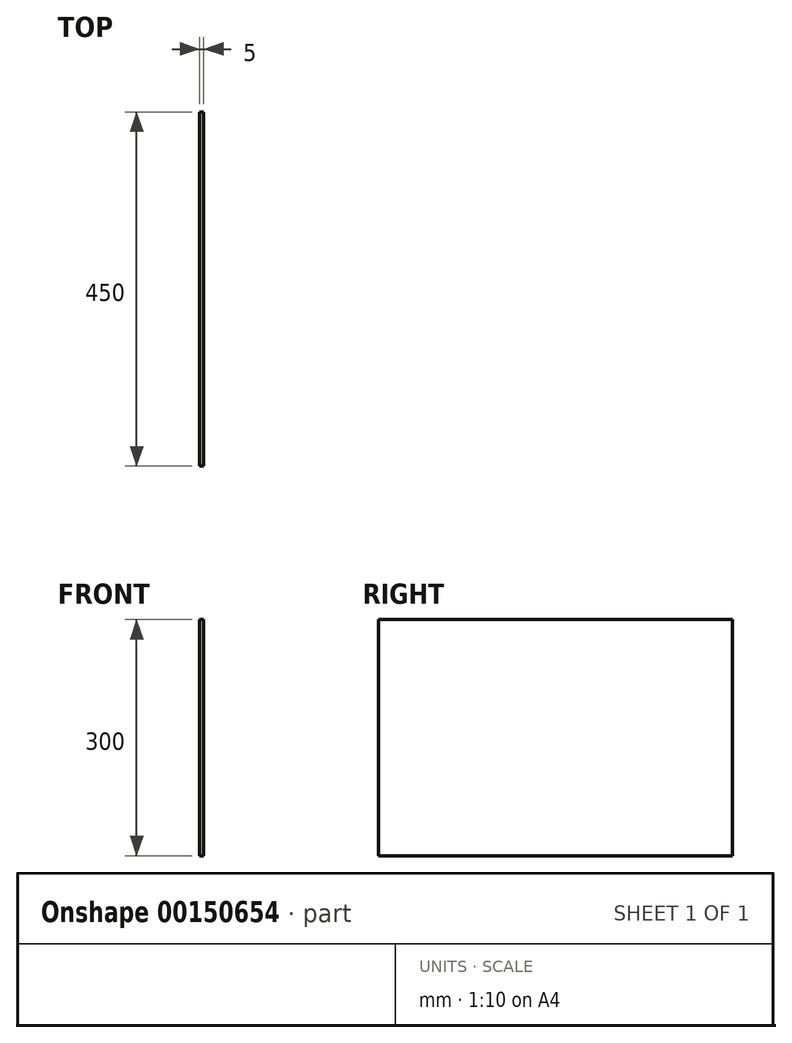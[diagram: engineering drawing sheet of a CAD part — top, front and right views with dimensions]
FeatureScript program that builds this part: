
annotation { "Feature Type Name" : "Feature", "Feature Type Description" : "" }
export const myFeature = defineFeature(function(context is Context, id is Id, definition is map)
    precondition{}
    {
        {
            var Q0;
            Q0=qCreatedBy(makeId("Right.planeOp"),FACE);
            var sketch = newSketch(context, id + "F0", { "sketchPlane" : qUnion([Q0])});
            skLineSegment(sketch, "E0.bottom", {"start": v(-222.97, -150) * mm, "end": v(227.03, -150) * mm});
            skLineSegment(sketch, "E0.top", {"start": v(-222.97, 150) * mm, "end": v(227.03, 150) * mm});
            skLineSegment(sketch, "E0.left", {"start": v(-222.97, -150) * mm, "end": v(-222.97, 150) * mm});
            skLineSegment(sketch, "E0.right", {"start": v(227.03, -150) * mm, "end": v(227.03, 150) * mm});
            skPoint(sketch, "E0.middle", {"position": v(2.03, 0) * mm});
            skSolve(sketch);
        }
        {
            var Q0;
            Q0 = qSketchRegion(id + "F0", true);
            extrude(context, id + "F1", {"entities" : qUnion([Q0]), "depth" : 5 * mm});
        }
    });
